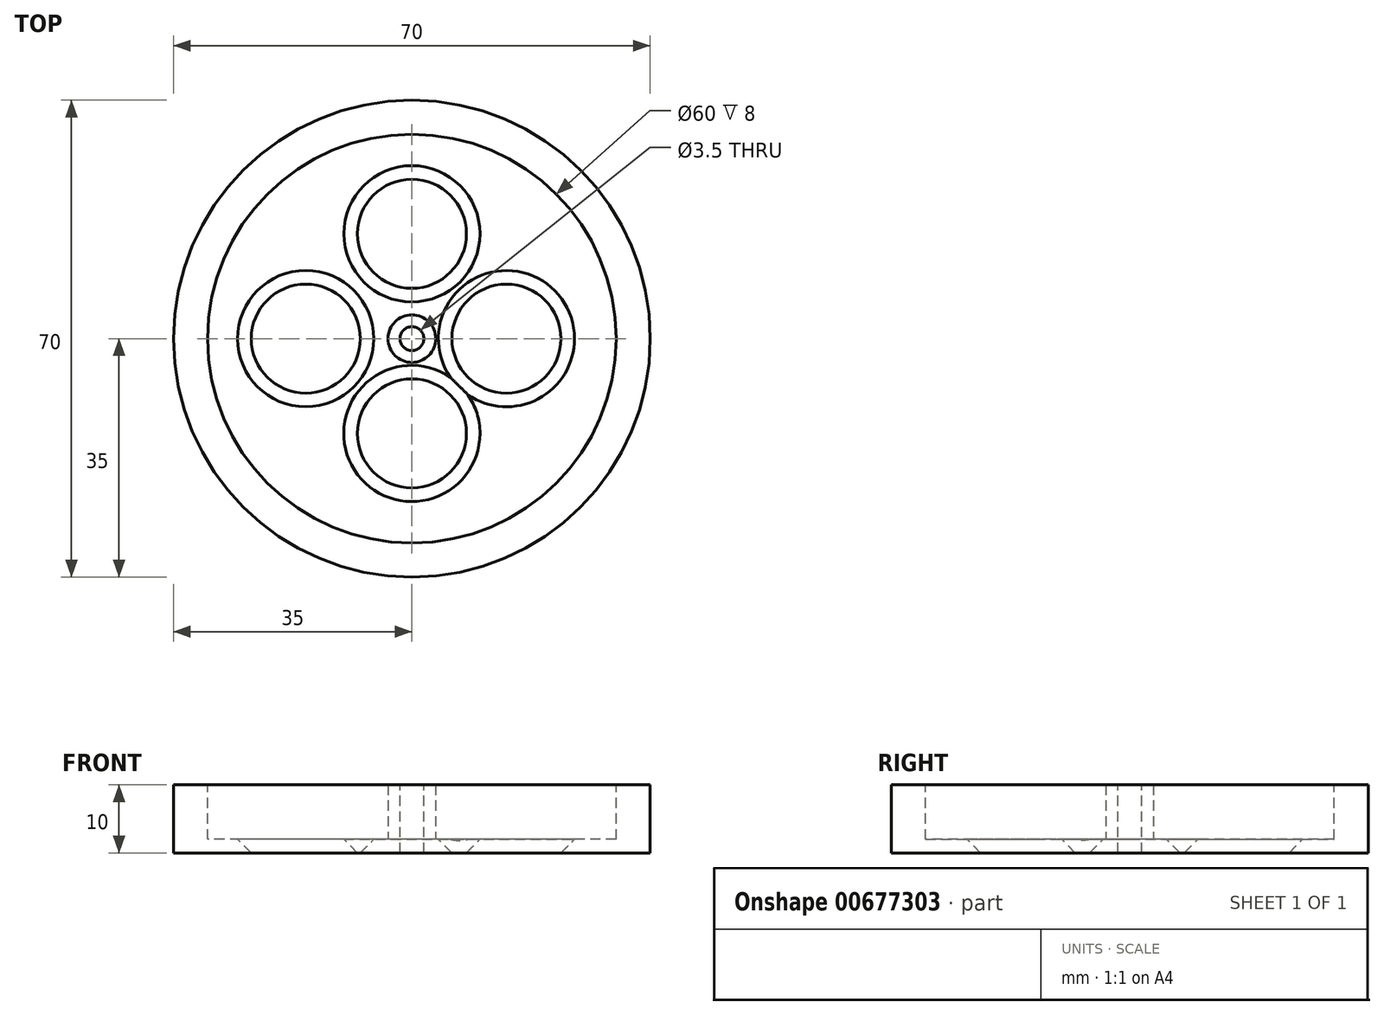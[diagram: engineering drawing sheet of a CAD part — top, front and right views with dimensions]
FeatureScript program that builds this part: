
annotation { "Feature Type Name" : "Feature", "Feature Type Description" : "" }
export const myFeature = defineFeature(function(context is Context, id is Id, definition is map)
    precondition{}
    {
        {
            var Q0;
            Q0=qCreatedBy(makeId("Top.planeOp"),FACE);
            var sketch = newSketch(context, id + "F0", { "sketchPlane" : qUnion([Q0])});
            skCircle(sketch, "E0", {"center": v(0, 0) * mm, "radius": 35 * mm});
            skSolve(sketch);
        }
        {
            var Q0;
            Q0=makeQuery(id+"F0.imprint","IMPRINT",FACE,{"disambiguationData":[TD([[makeQuery(id+"F0.imprint","IMPRINT",EDGE,{"derivedFrom":sQuery(id+"F0.wireOp",EDGE,"E0")}),1.0]])]});
            extrude(context, id + "F1", {"entities" : qUnion([Q0]), "depth" : 10 * mm, "offsetDistance" : 25 * mm});
        }
        {
            var Q0;
            Q0=makeQuery(id+"F1.opExtrude","CAP_FACE",FACE,{"disambiguationData":[OSD([sQuery(id+"F0.wireOp",EDGE,"E0")])],"isStart":false});
            var sketch = newSketch(context, id + "F2", { "sketchPlane" : qUnion([Q0])});
            skCircle(sketch, "E1", {"center": v(0, 0) * mm, "radius": 30 * mm});
            skSolve(sketch);
        }
        {
            var Q0;
            Q0=makeQuery(id+"F2.imprint","IMPRINT",FACE,{"disambiguationData":[TD([[makeQuery(id+"F2.imprint","IMPRINT",EDGE,{"derivedFrom":sQuery(id+"F2.wireOp",EDGE,"E1")}),1.0]])]});
            var Q1;
            Q1=sQuery(id+"F2.wireOp",EDGE,"E1");
            extrude(context, id + "F3", {"entities" : qUnion([Q0]), "operationType" : NewBodyOperationType.REMOVE, "surfaceEntities" : qUnion([Q1]), "oppositeDirection" : true, "depth" : 8 * mm, "offsetDistance" : 25 * mm});
        }
        {
            var Q0;
            Q0=makeQuery(id+"F3.boolean.opBoolean","COPY",FACE,{"derivedFrom":makeQuery(id+"F3.opExtrude","CAP_FACE",FACE,{"disambiguationData":[OSD([sQuery(id+"F2.wireOp",EDGE,"E1")])],"isStart":false})});
            var sketch = newSketch(context, id + "F4", { "sketchPlane" : qUnion([Q0])});
            skPoint(sketch, "E2", {"position": v(-17.78, 0) * mm});
            skPoint(sketch, "E3", {"position": v(0, -13.92) * mm});
            skPoint(sketch, "E4", {"position": v(13.88, 0) * mm});
            skPoint(sketch, "E5", {"position": v(0, 15.4) * mm});
            skSolve(sketch);
        }
        {
            var Q0;
            Q0=sQuery(id+"F4.wireOp",VERTEX,"E5");
            var Q1;
            Q1=sQuery(id+"F4.wireOp",VERTEX,"E4");
            var Q2;
            Q2=sQuery(id+"F4.wireOp",VERTEX,"E3");
            var Q3;
            Q3=makeQuery(id+"F1.opExtrude","SWEPT_BODY",BODY,{"disambiguationData":[OSD([sQuery(id+"F0.wireOp",EDGE,"E0")])]});
            hole(context, id + "F5", {"style" : HoleStyle.C_SINK, "endStyle" : HoleEndStyle.THROUGH, "holeDiameter" : 5 * mm, "cSinkDiameter" : 20 * mm, "cSinkAngle" : 90 * degree, "majorDiameter" : 5 * mm, "isTappedThrough" : true, "tappedDepth" : 12 * mm, "tapClearance" : 3, "locations" : qUnion([Q0, Q1, Q2]), "scope" : qUnion([Q3])});
        }
        {
            var Q0;
            Q0=makeQuery(id+"F3.boolean.opBoolean","COPY",FACE,{"derivedFrom":makeQuery(id+"F3.opExtrude","CAP_FACE",FACE,{"disambiguationData":[OSD([sQuery(id+"F2.wireOp",EDGE,"E1")])],"isStart":false})});
            var sketch = newSketch(context, id + "F6", { "sketchPlane" : qUnion([Q0])});
            skPoint(sketch, "E6", {"position": v(-15.59, 0) * mm});
            skSolve(sketch);
        }
        {
            var Q0;
            Q0=sQuery(id+"F6.wireOp",VERTEX,"E6");
            var Q1;
            Q1=makeQuery(id+"F1.opExtrude","SWEPT_BODY",BODY,{"disambiguationData":[OSD([sQuery(id+"F0.wireOp",EDGE,"E0")])]});
            hole(context, id + "F7", {"style" : HoleStyle.C_SINK, "endStyle" : HoleEndStyle.THROUGH, "holeDiameter" : 5 * mm, "cSinkDiameter" : 20 * mm, "cSinkAngle" : 90 * degree, "majorDiameter" : 5 * mm, "isTappedThrough" : true, "tappedDepth" : 12 * mm, "tapClearance" : 3, "locations" : qUnion([Q0]), "scope" : qUnion([Q1])});
        }
        {
            var Q0;
            Q0=makeQuery(id+"F3.boolean.opBoolean","COPY",FACE,{"derivedFrom":makeQuery(id+"F3.opExtrude","CAP_FACE",FACE,{"disambiguationData":[OSD([sQuery(id+"F2.wireOp",EDGE,"E1")])],"isStart":false})});
            var sketch = newSketch(context, id + "F8", { "sketchPlane" : qUnion([Q0])});
            skCircle(sketch, "E7", {"center": v(0, 0) * mm, "radius": 3.5 * mm});
            skSolve(sketch);
        }
        {
            var Q0;
            Q0=makeQuery(id+"F8.imprint","IMPRINT",FACE,{"disambiguationData":[TD([[makeQuery(id+"F8.imprint","IMPRINT",EDGE,{"derivedFrom":sQuery(id+"F8.wireOp",EDGE,"E7")}),1.0]])]});
            extrude(context, id + "F9", {"entities" : qUnion([Q0]), "operationType" : NewBodyOperationType.ADD, "depth" : 8 * mm, "offsetDistance" : 25 * mm});
        }
        {
            var Q0;
            Q0=makeQuery(id+"F9.opExtrude","CAP_FACE",FACE,{"disambiguationData":[OSD([sQuery(id+"F8.wireOp",EDGE,"E7")])],"isStart":false});
            var sketch = newSketch(context, id + "F10", { "sketchPlane" : qUnion([Q0])});
            skPoint(sketch, "E8", {"position": v(0, 0) * mm});
            skSolve(sketch);
        }
        {
            var Q0;
            Q0=sQuery(id+"F10.wireOp",VERTEX,"E8");
            var Q1;
            Q1=makeQuery(id+"F1.opExtrude","SWEPT_BODY",BODY,{"disambiguationData":[OSD([sQuery(id+"F0.wireOp",EDGE,"E0")])]});
            hole(context, id + "F11", {"style" : HoleStyle.SIMPLE, "endStyle" : HoleEndStyle.THROUGH, "holeDiameter" : 3.5 * mm, "majorDiameter" : 5 * mm, "isTappedThrough" : true, "tappedDepth" : 12 * mm, "tapClearance" : 3, "locations" : qUnion([Q0]), "scope" : qUnion([Q1])});
        }
    });
